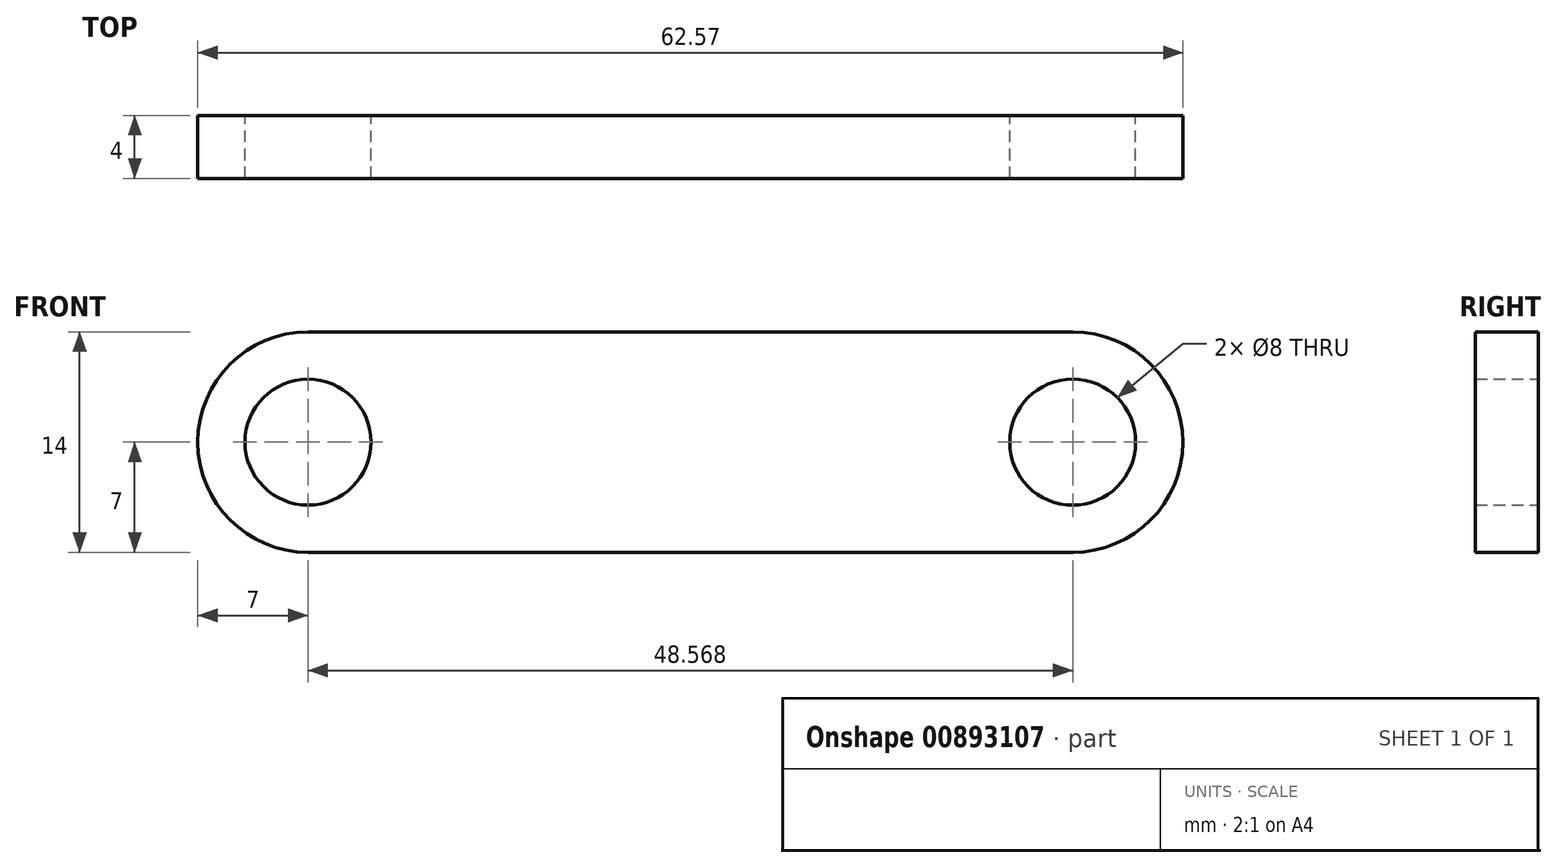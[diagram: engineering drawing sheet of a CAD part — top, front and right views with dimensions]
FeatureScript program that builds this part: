
annotation { "Feature Type Name" : "Feature", "Feature Type Description" : "" }
export const myFeature = defineFeature(function(context is Context, id is Id, definition is map)
    precondition{}
    {
        {
            assignVariable(context, id + "F0", {"name" : "Thickness", "anyValue" : 4});
        }
        {
            var Q0;
            Q0=qCreatedBy(makeId("Front.planeOp"),FACE);
            var sketch = newSketch(context, id + "F1", { "sketchPlane" : qUnion([Q0])});
            skCircle(sketch, "E0", {"center": v(0, 0) * mm, "radius": 4 * mm});
            skCircle(sketch, "E1", {"center": v(48.57, 0) * mm, "radius": 4 * mm});
            skArc(sketch, "E2", {"start": v(48.57, -7) * mm, "mid": v(55.57, 0) * mm, "end": v(48.57, 7) * mm});
            skArc(sketch, "E3", {"start": v(0, 7) * mm, "mid": v(-7, 0) * mm, "end": v(0, -7) * mm});
            skLineSegment(sketch, "E4", {"start": v(0, 7) * mm, "end": v(48.57, 7) * mm});
            skLineSegment(sketch, "E5", {"start": v(0, -7) * mm, "end": v(48.57, -7) * mm});
            skSolve(sketch);
        }
        {
            var Q0;
            Q0=makeQuery(id+"F1.imprint","IMPRINT",FACE,{"disambiguationData":[TD([[makeQuery(id+"F1.imprint","IMPRINT",EDGE,{"derivedFrom":sQuery(id+"F1.wireOp",EDGE,"E0")}),-1.0]])]});
            extrude(context, id + "F2", {"entities" : qUnion([Q0]), "depth" : (getVariable(context, 'Thickness')) * mm, "offsetDistance" : 25 * mm});
        }
    });
